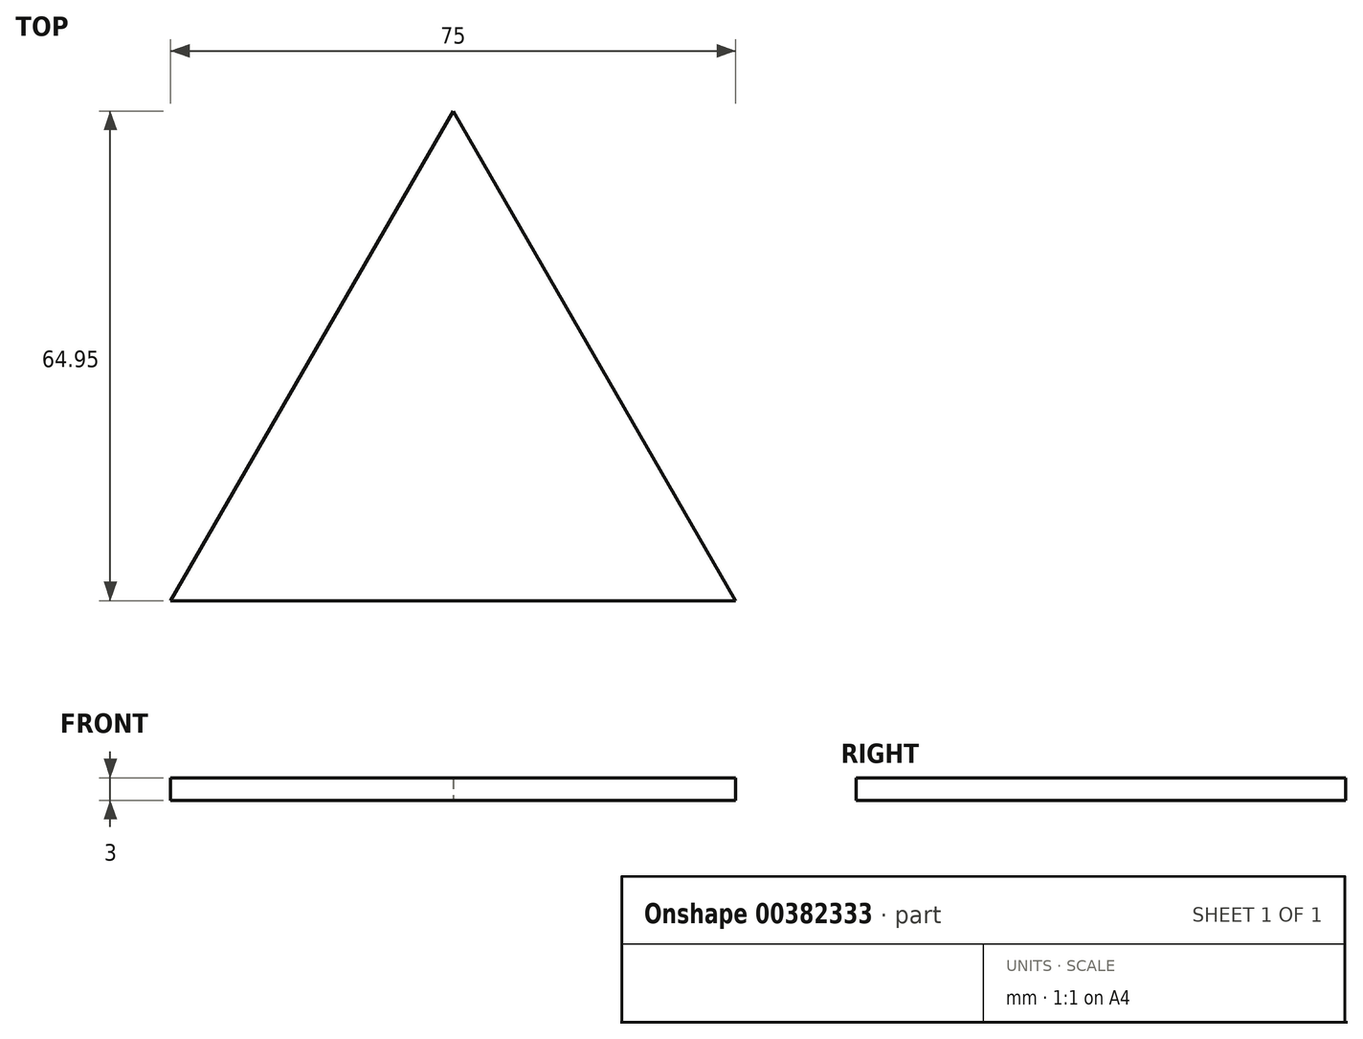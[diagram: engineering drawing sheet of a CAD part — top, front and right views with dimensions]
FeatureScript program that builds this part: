
annotation { "Feature Type Name" : "Feature", "Feature Type Description" : "" }
export const myFeature = defineFeature(function(context is Context, id is Id, definition is map)
    precondition{}
    {
        {
            var Q0;
            Q0=qCreatedBy(makeId("Top.planeOp"),FACE);
            var sketch = newSketch(context, id + "F0", { "sketchPlane" : qUnion([Q0])});
            skLineSegment(sketch, "E0", {"start": v(-24.95, 0) * mm, "end": v(50.05, 0) * mm});
            skLineSegment(sketch, "E1", {"start": v(50.05, 0) * mm, "end": v(12.55, 64.95) * mm});
            skPoint(sketch, "E1.endSnap0", {"position": v(12.55, 0) * mm});
            skLineSegment(sketch, "E2", {"start": v(12.55, 64.95) * mm, "end": v(-24.95, 0) * mm});
            skSolve(sketch);
        }
        {
            var Q0;
            Q0=makeQuery(id+"F0.imprint","IMPRINT",FACE,{"disambiguationData":[TD([[makeQuery(id+"F0.imprint","IMPRINT",EDGE,{"derivedFrom":sQuery(id+"F0.wireOp",EDGE,"E0")}),1.0]])]});
            extrude(context, id + "F1", {"entities" : qUnion([Q0]), "depth" : 3 * mm, "offsetDistance" : 25 * mm});
        }
    });
